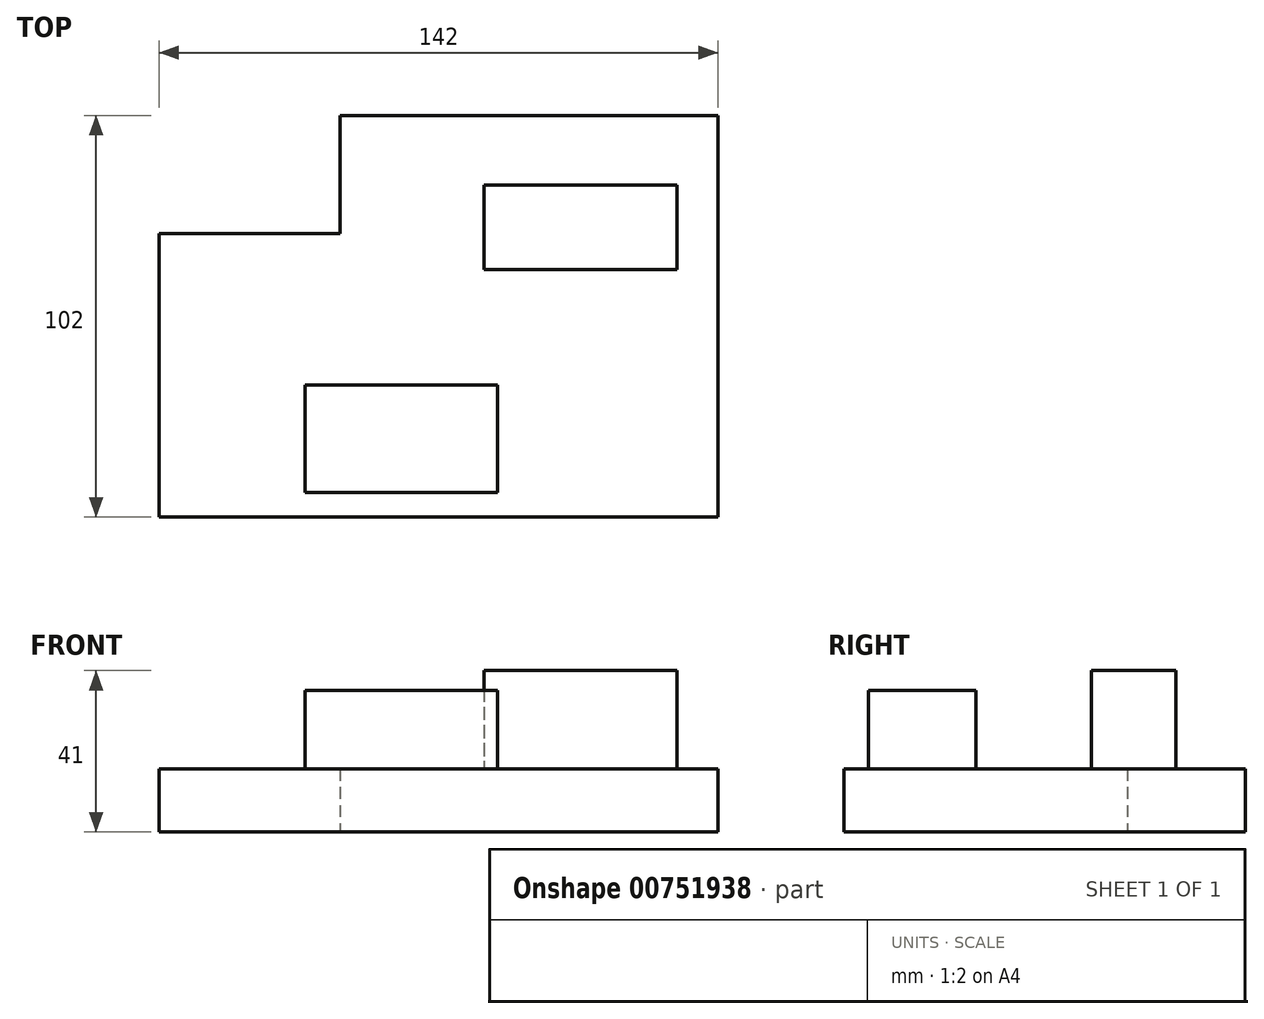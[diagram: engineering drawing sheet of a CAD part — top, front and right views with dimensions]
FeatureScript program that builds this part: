
annotation { "Feature Type Name" : "Feature", "Feature Type Description" : "" }
export const myFeature = defineFeature(function(context is Context, id is Id, definition is map)
    precondition{}
    {
        {
            var Q0;
            Q0=qCreatedBy(makeId("Top.planeOp"),FACE);
            var sketch = newSketch(context, id + "F0", { "sketchPlane" : qUnion([Q0])});
            skLineSegment(sketch, "E0", {"start": v(-8.12, 57.8) * mm, "end": v(-8.12, 27.8) * mm});
            skLineSegment(sketch, "E1", {"start": v(-8.12, 27.8) * mm, "end": v(-54.12, 27.8) * mm});
            skLineSegment(sketch, "E2", {"start": v(-54.12, 27.8) * mm, "end": v(-54.12, -44.2) * mm});
            skLineSegment(sketch, "E3", {"start": v(-54.12, -44.2) * mm, "end": v(87.88, -44.2) * mm});
            skLineSegment(sketch, "E4", {"start": v(87.88, -44.2) * mm, "end": v(87.88, 57.8) * mm});
            skLineSegment(sketch, "E5", {"start": v(87.88, 57.8) * mm, "end": v(-8.12, 57.8) * mm});
            skSolve(sketch);
        }
        {
            var Q0;
            Q0=makeQuery(id+"F0.imprint","IMPRINT",FACE,{"disambiguationData":[TD([[makeQuery(id+"F0.imprint","IMPRINT",EDGE,{"derivedFrom":sQuery(id+"F0.wireOp",EDGE,"E0")}),1.0]])]});
            extrude(context, id + "F1", {"entities" : qUnion([Q0]), "depth" : 16 * mm, "offsetDistance" : 25 * mm});
        }
        {
            var Q0;
            Q0=makeQuery(id+"F1.opExtrude","CAP_FACE",FACE,{"disambiguationData":[OSD([sQuery(id+"F0.wireOp",EDGE,"E0"),sQuery(id+"F0.wireOp",EDGE,"E1"),sQuery(id+"F0.wireOp",EDGE,"E2"),sQuery(id+"F0.wireOp",EDGE,"E3"),sQuery(id+"F0.wireOp",EDGE,"E4"),sQuery(id+"F0.wireOp",EDGE,"E5")])],"isStart":false});
            var sketch = newSketch(context, id + "F2", { "sketchPlane" : qUnion([Q0])});
            skLineSegment(sketch, "E6.bottom", {"start": v(28.48, 40.22) * mm, "end": v(77.47, 40.22) * mm});
            skLineSegment(sketch, "E6.top", {"start": v(28.48, 18.75) * mm, "end": v(77.47, 18.75) * mm});
            skLineSegment(sketch, "E6.left", {"start": v(28.48, 40.22) * mm, "end": v(28.48, 18.75) * mm});
            skLineSegment(sketch, "E6.right", {"start": v(77.47, 40.22) * mm, "end": v(77.47, 18.75) * mm});
            skSolve(sketch);
        }
        {
            var Q0;
            Q0=makeQuery(id+"F2.imprint","IMPRINT",FACE,{"disambiguationData":[TD([[makeQuery(id+"F2.imprint","IMPRINT",EDGE,{"derivedFrom":sQuery(id+"F2.wireOp",EDGE,"E6.bottom")}),-1.0]])]});
            extrude(context, id + "F3", {"entities" : qUnion([Q0]), "operationType" : NewBodyOperationType.ADD, "depth" : 25 * mm, "offsetDistance" : 25 * mm});
        }
        {
            var Q0;
            Q0=makeQuery(id+"F1.opExtrude","CAP_FACE",FACE,{"disambiguationData":[OSD([sQuery(id+"F0.wireOp",EDGE,"E0"),sQuery(id+"F0.wireOp",EDGE,"E1"),sQuery(id+"F0.wireOp",EDGE,"E2"),sQuery(id+"F0.wireOp",EDGE,"E3"),sQuery(id+"F0.wireOp",EDGE,"E4"),sQuery(id+"F0.wireOp",EDGE,"E5")])],"isStart":false});
            var sketch = newSketch(context, id + "F4", { "sketchPlane" : qUnion([Q0])});
            skLineSegment(sketch, "E7.bottom", {"start": v(-16.96, -10.6) * mm, "end": v(31.84, -10.6) * mm});
            skLineSegment(sketch, "E7.top", {"start": v(-16.96, -37.95) * mm, "end": v(31.84, -37.95) * mm});
            skLineSegment(sketch, "E7.left", {"start": v(-16.96, -10.6) * mm, "end": v(-16.96, -37.95) * mm});
            skLineSegment(sketch, "E7.right", {"start": v(31.84, -10.6) * mm, "end": v(31.84, -37.95) * mm});
            skSolve(sketch);
        }
        {
            var Q0;
            Q0=makeQuery(id+"F4.imprint","IMPRINT",FACE,{"disambiguationData":[TD([[makeQuery(id+"F4.imprint","IMPRINT",EDGE,{"derivedFrom":sQuery(id+"F4.wireOp",EDGE,"E7.bottom")}),-1.0]])]});
            extrude(context, id + "F5", {"entities" : qUnion([Q0]), "operationType" : NewBodyOperationType.ADD, "depth" : 20 * mm, "offsetDistance" : 25 * mm});
        }
    });
